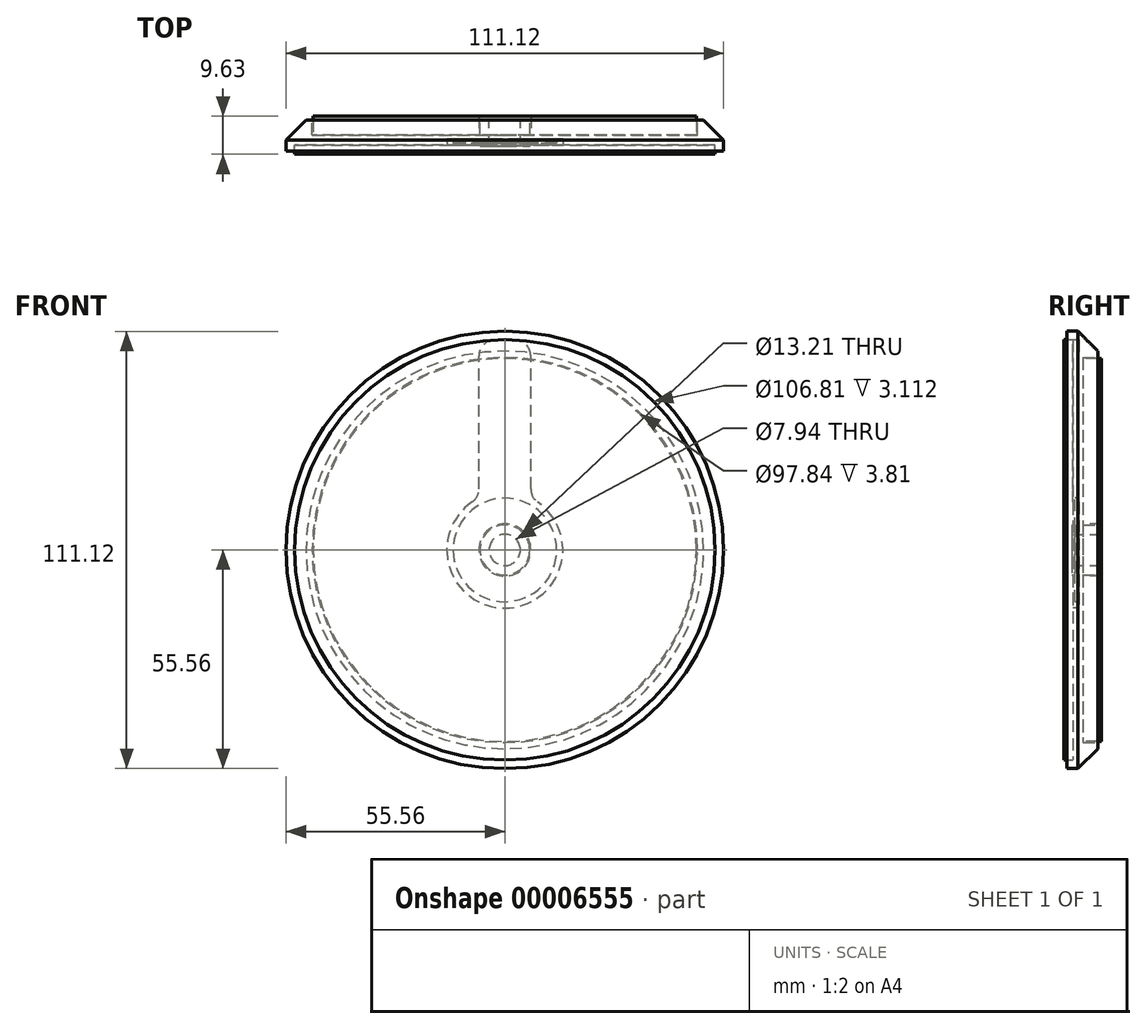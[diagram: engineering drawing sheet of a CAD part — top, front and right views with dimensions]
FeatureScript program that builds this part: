
annotation { "Feature Type Name" : "Feature", "Feature Type Description" : "" }
export const myFeature = defineFeature(function(context is Context, id is Id, definition is map)
    precondition{}
    {
        {
            var Q0;
            Q0=qCreatedBy(makeId("Top.planeOp"),FACE);
            var sketch = newSketch(context, id + "F0", { "sketchPlane" : qUnion([Q0])});
            skLineSegment(sketch, "E0.rect.bottom", {"start": v(0, -15.56) * mm, "end": v(-50.48, -15.56) * mm});
            skLineSegment(sketch, "E0.rect.top", {"start": v(55.56, 15.56) * mm, "end": v(9.98, 15.56) * mm});
            skLineSegment(sketch, "E0.rect.left", {"start": v(55.56, -15.56) * mm, "end": v(55.56, 15.56) * mm});
            skLineSegment(sketch, "E0.rect.right", {"start": v(-55.56, -10.48) * mm, "end": v(-55.56, 15.56) * mm});
            skPoint(sketch, "E0.rect.middle", {"position": v(0, 0) * mm});
            skLineSegment(sketch, "E1.rect.bottom", {"start": v(-4, -4.68) * mm, "end": v(-5.02, -4.68) * mm});
            skLineSegment(sketch, "E1.rect.right", {"start": v(-5.02, -4.68) * mm, "end": v(-5.02, -2.31) * mm});
            skPoint(sketch, "E1.rect.middle", {"position": v(0, -3.56) * mm});
            skLineSegment(sketch, "E2.rect.right", {"start": v(-8, 12.4) * mm, "end": v(-8, 16.42) * mm});
            skPoint(sketch, "E2.rect.middle", {"position": v(0, 14.4) * mm});
            skLineSegment(sketch, "E3.0", {"start": v(-9.98, 15.56) * mm, "end": v(-9.98, 16.42) * mm});
            skLineSegment(sketch, "E4.1", {"start": v(7, -7.04) * mm, "end": v(6.35, -7.04) * mm});
            skLineSegment(sketch, "E5", {"start": v(-9.98, 16.42) * mm, "end": v(-8, 16.42) * mm});
            skLineSegment(sketch, "E6.trimOffspring", {"start": v(-9.98, 15.56) * mm, "end": v(-49.34, 15.56) * mm});
            skLineSegment(sketch, "E7.rect.bottom", {"start": v(42.88, -12.38) * mm, "end": v(11.25, -12.38) * mm});
            skLineSegment(sketch, "E7.rect.top", {"start": v(42.88, 15.56) * mm, "end": v(11.25, 15.56) * mm});
            skLineSegment(sketch, "E7.rect.left", {"start": v(42.88, -12.38) * mm, "end": v(42.88, 15.56) * mm});
            skLineSegment(sketch, "E7.rect.right", {"start": v(11.25, -12.38) * mm, "end": v(11.25, 15.56) * mm});
            skPoint(sketch, "E7.rect.middle", {"position": v(27.06, 1.59) * mm});
            skLineSegment(sketch, "E8.rect.bottom", {"start": v(11.25, -9.41) * mm, "end": v(9.27, -9.41) * mm});
            skLineSegment(sketch, "E8.rect.top", {"start": v(11.25, 12.59) * mm, "end": v(9.27, 12.59) * mm});
            skLineSegment(sketch, "E8.rect.left", {"start": v(11.25, -9.41) * mm, "end": v(11.25, 12.59) * mm});
            skLineSegment(sketch, "E8.rect.right", {"start": v(9.27, -9.41) * mm, "end": v(9.27, 12.59) * mm});
            skPoint(sketch, "E8.rect.middle", {"position": v(10.26, 1.59) * mm});
            skLineSegment(sketch, "E9", {"start": v(10.26, 1.59) * mm, "end": v(-17.78, 1.59) * mm});
            skLineSegment(sketch, "E10", {"start": v(-55.56, -10.48) * mm, "end": v(-55.56, -9.46) * mm});
            skLineSegment(sketch, "E11", {"start": v(-55.56, -9.46) * mm, "end": v(-52.39, -9.46) * mm});
            skLineSegment(sketch, "E12", {"start": v(-52.39, -9.46) * mm, "end": v(-52.39, -6) * mm});
            skLineSegment(sketch, "E13", {"start": v(-52.39, -6) * mm, "end": v(-53.53, -6) * mm});
            skLineSegment(sketch, "E14", {"start": v(-53.53, -6) * mm, "end": v(-53.53, -4.42) * mm});
            skLineSegment(sketch, "E15", {"start": v(-53.53, -4.42) * mm, "end": v(-50.8, -4.42) * mm});
            skLineSegment(sketch, "E16", {"start": v(-50.8, -4.42) * mm, "end": v(-50.8, -13.02) * mm});
            skLineSegment(sketch, "E17", {"start": v(-50.8, -13.02) * mm, "end": v(-6.35, -13.02) * mm});
            skLineSegment(sketch, "E18", {"start": v(-53.66, -4.42) * mm, "end": v(-53.66, -9.46) * mm});
            skLineSegment(sketch, "E19", {"start": v(-55.56, -10.48) * mm, "end": v(-50.48, -15.56) * mm});
            skPoint(sketch, "E20.orphan", {"position": v(-55.56, -15.56) * mm});
            skLineSegment(sketch, "E21", {"start": v(55.56, -13.9) * mm, "end": v(4.5, -13.9) * mm});
            skLineSegment(sketch, "E22", {"start": v(-6.35, 16.68) * mm, "end": v(-48.32, 16.68) * mm});
            skLineSegment(sketch, "E23", {"start": v(-55.56, 17.97) * mm, "end": v(-50.5, 23.03) * mm});
            skPoint(sketch, "E24.orphan", {"position": v(-55.59, 23.03) * mm});
            skLineSegment(sketch, "E25.rect.bottom", {"start": v(-74.76, -10.55) * mm, "end": v(-76.24, -10.55) * mm});
            skLineSegment(sketch, "E25.rect.top", {"start": v(-74.76, 9.87) * mm, "end": v(-76.24, 9.87) * mm});
            skLineSegment(sketch, "E25.rect.left", {"start": v(-74.76, -10.55) * mm, "end": v(-74.76, 9.87) * mm});
            skLineSegment(sketch, "E25.rect.right", {"start": v(-76.24, -10.55) * mm, "end": v(-76.24, 9.87) * mm});
            skPoint(sketch, "E25.rect.middle", {"position": v(-75.5, -0.34) * mm});
            skLineSegment(sketch, "E26.bottom", {"start": v(-76.24, 7.41) * mm, "end": v(-74.76, 7.41) * mm});
            skLineSegment(sketch, "E26.top", {"start": v(-76.24, -3.8) * mm, "end": v(-74.76, -3.8) * mm});
            skLineSegment(sketch, "E26.left", {"start": v(-76.24, 7.41) * mm, "end": v(-76.24, -3.8) * mm});
            skLineSegment(sketch, "E26.right", {"start": v(-74.76, 7.41) * mm, "end": v(-74.76, -3.8) * mm});
            skLineSegment(sketch, "E27", {"start": v(-48.92, 23.03) * mm, "end": v(-48.92, 19.22) * mm});
            skLineSegment(sketch, "E28", {"start": v(-48.92, 19.22) * mm, "end": v(-6.35, 19.22) * mm});
            skLineSegment(sketch, "E29", {"start": v(-6.35, 19.22) * mm, "end": v(-6.35, 23.05) * mm});
            skLineSegment(sketch, "E30.trimOffspring", {"start": v(-6.35, 23.05) * mm, "end": v(-3.97, 23.05) * mm});
            skLineSegment(sketch, "E31", {"start": v(-50.5, 23.03) * mm, "end": v(-48.92, 23.03) * mm});
            skLineSegment(sketch, "E32", {"start": v(0, 23.05) * mm, "end": v(0, 16.68) * mm});
            skLineSegment(sketch, "E33", {"start": v(0, 12.42) * mm, "end": v(0, 9.24) * mm});
            skLineSegment(sketch, "E34", {"start": v(-53.53, -4.3) * mm, "end": v(-50.55, -4.3) * mm});
            skLineSegment(sketch, "E35", {"start": v(-53.53, -2.31) * mm, "end": v(-53.53, -4.3) * mm});
            skLineSegment(sketch, "E36", {"start": v(0, -4.68) * mm, "end": v(0, -7.04) * mm});
            skLineSegment(sketch, "E37", {"start": v(-45.33, 1.8) * mm, "end": v(-74.76, 1.8) * mm});
            skLineSegment(sketch, "E38", {"start": v(11.25, -10.9) * mm, "end": v(9.27, -10.9) * mm});
            skLineSegment(sketch, "E39", {"start": v(9.27, -10.9) * mm, "end": v(7.77, -10.9) * mm});
            skLineSegment(sketch, "E40", {"start": v(-55.56, 17.97) * mm, "end": v(-55.56, 15.11) * mm});
            skLineSegment(sketch, "E41.trimOffspring", {"start": v(0, -7.04) * mm, "end": v(-7, -7.04) * mm});
            skLineSegment(sketch, "E42", {"start": v(-74.76, 7.41) * mm, "end": v(-74.76, 10.59) * mm});
            skLineSegment(sketch, "E43", {"start": v(-53.66, -4.42) * mm, "end": v(-53.66, 10.16) * mm});
            skLineSegment(sketch, "E44", {"start": v(-55.56, 15.11) * mm, "end": v(-53.4, 15.11) * mm});
            skLineSegment(sketch, "E45", {"start": v(-53.4, 15.11) * mm, "end": v(-53.4, 16.68) * mm});
            skLineSegment(sketch, "E46", {"start": v(-55.56, 14.1) * mm, "end": v(-52.39, 14.1) * mm});
            skLineSegment(sketch, "E47", {"start": v(-52.39, 14.1) * mm, "end": v(-52.39, 15.56) * mm});
            skLineSegment(sketch, "E48", {"start": v(-52.39, 15.56) * mm, "end": v(-49.34, 15.56) * mm});
            skLineSegment(sketch, "E49", {"start": v(-48.32, 16.68) * mm, "end": v(-53.4, 16.68) * mm});
            skLineSegment(sketch, "E50", {"start": v(-6.35, 16.68) * mm, "end": v(-6.35, 16.42) * mm});
            skLineSegment(sketch, "E51", {"start": v(-6.35, 16.42) * mm, "end": v(-3.97, 16.42) * mm});
            skLineSegment(sketch, "E52", {"start": v(0, 16.42) * mm, "end": v(0, 16.68) * mm});
            skLineSegment(sketch, "E53", {"start": v(-7.56, -2.31) * mm, "end": v(-53.53, -2.31) * mm});
            skLineSegment(sketch, "E54", {"start": v(-50.55, -4.3) * mm, "end": v(-50.55, -5.87) * mm});
            skLineSegment(sketch, "E55", {"start": v(-50.55, -5.87) * mm, "end": v(-50.55, -7.04) * mm});
            skLineSegment(sketch, "E56", {"start": v(-50.55, -7.04) * mm, "end": v(-7, -7.04) * mm});
            skLineSegment(sketch, "E57", {"start": v(-6.35, -13.02) * mm, "end": v(-6.35, -7.62) * mm});
            skLineSegment(sketch, "E58", {"start": v(-6.35, -7.62) * mm, "end": v(-3.97, -7.62) * mm});
            skLineSegment(sketch, "E59", {"start": v(-45.33, 1.8) * mm, "end": v(-45.33, -2.31) * mm});
            skLineSegment(sketch, "E60", {"start": v(0, -7.62) * mm, "end": v(6.35, -7.62) * mm});
            skLineSegment(sketch, "E61", {"start": v(-4, -4.68) * mm, "end": v(-4, -4.93) * mm});
            skLineSegment(sketch, "E62", {"start": v(-4, -4.93) * mm, "end": v(0, -4.93) * mm});
            skLineSegment(sketch, "E63", {"start": v(-6.41, 12.4) * mm, "end": v(-6.41, 12.14) * mm});
            skLineSegment(sketch, "E64.trimOffspring", {"start": v(-6.41, 12.4) * mm, "end": v(-8, 12.4) * mm});
            skLineSegment(sketch, "E65", {"start": v(0, -1.42) * mm, "end": v(0, 10.58) * mm});
            skLineSegment(sketch, "E66", {"start": v(0, -1.42) * mm, "end": v(0, 4.58) * mm});
            skLineSegment(sketch, "E67", {"start": v(-6.41, 10.83) * mm, "end": v(-53.66, 10.83) * mm});
            skLineSegment(sketch, "E68", {"start": v(-53.66, 10.83) * mm, "end": v(-53.66, 10.16) * mm});
            skLineSegment(sketch, "E69", {"start": v(-5.02, -2.31) * mm, "end": v(-5.02, -1.68) * mm});
            skLineSegment(sketch, "E70", {"start": v(-5.02, -1.68) * mm, "end": v(-7.56, -1.68) * mm});
            skLineSegment(sketch, "E71", {"start": v(-7.56, -1.68) * mm, "end": v(-7.56, -2.31) * mm});
            skLineSegment(sketch, "E72", {"start": v(-6.41, 12.14) * mm, "end": v(-6.41, 10.83) * mm});
            skPoint(sketch, "E73.end.orphan", {"position": v(0, 12.14) * mm});
            skPoint(sketch, "E74.orphan", {"position": v(0, 10.83) * mm});
            skLineSegment(sketch, "E75", {"start": v(-3.97, 23.05) * mm, "end": v(-3.97, 16.42) * mm});
            skLineSegment(sketch, "E76", {"start": v(-3.97, -7.62) * mm, "end": v(-3.97, -15.56) * mm});
            skPoint(sketch, "E77.start.orphan", {"position": v(0, -13.02) * mm});
            skSolve(sketch);
        }
        {
            var Q0;
            Q0=makeQuery(id+"F0.imprint","IMPRINT",FACE,{"disambiguationData":[TD([[makeQuery(id+"F0.imprint","IMPRINT",EDGE,{"derivedFrom":sQuery(id+"F0.wireOp",EDGE,"E22")}),-1.0]])]});
            var Q1;
            Q1=sQuery(id+"F0.wireOp",EDGE,"E32");
            revolve(context, id + "F1", {"entities" : qUnion([Q0]), "axis" : qUnion([Q1]), "revolveType" : RevolveType.FULL});
        }
        {
            var Q0;
            Q0=makeQuery(id+"F1.opRevolve","SWEPT_FACE",FACE,{"disambiguationData":[OSD([sQuery(id+"F0.wireOp",EDGE,"E28")])]});
            var sketch = newSketch(context, id + "F2", { "sketchPlane" : qUnion([Q0])});
            skCircle(sketch, "E78.0", {"center": v(0, 0) * mm, "radius": 6.35 * mm});
            skCircle(sketch, "E79.0", {"center": v(0, 0) * mm, "radius": 48.92 * mm});
            skCircle(sketch, "E80.0", {"center": v(0, 0) * mm, "radius": 48.67 * mm});
            skCircle(sketch, "E81.0", {"center": v(0, 0) * mm, "radius": 6.6 * mm});
            skSolve(sketch);
        }
        {
            var Q0;
            Q0=makeQuery(id+"F2.imprint","IMPRINT",FACE,{"disambiguationData":[TD([[makeQuery(id+"F2.imprint","IMPRINT",EDGE,{"derivedFrom":sQuery(id+"F2.wireOp",EDGE,"E80.0")}),1.0]])]});
            extrude(context, id + "F3", {"entities" : qUnion([Q0]), "depth" : 4.76 * mm});
        }
        {
            var Q0;
            Q0=makeQuery(id+"F1.opRevolve","SWEPT_FACE",FACE,{"disambiguationData":[OSD([sQuery(id+"F0.wireOp",EDGE,"E44")])]});
            var sketch = newSketch(context, id + "F4", { "sketchPlane" : qUnion([Q0])});
            skSolve(sketch);
        }
        {
            var Q0;
            {var subQ0=sQuery(id+"F0.wireOp",EDGE,"E44");Q0=makeQuery(id+"F4.imprint","IMPRINT",FACE,{"disambiguationData":[TD([[makeQuery(id+"F4.imprint","IMPRINT",EDGE,{"derivedFrom":makeQuery(id+"F1.opRevolve","SWEPT_EDGE",EDGE,{"disambiguationData":[OSD([sQuery(id+"F0.wireOp",EDGE,"E40"),subQ0])]})}),-1.0]])]});}
            extrude(context, id + "F5", {"entities" : qUnion([Q0]), "operationType" : NewBodyOperationType.ADD, "depth" : 0.76 * mm});
        }
        {
            var Q0;
            Q0=makeQuery(id+"F1.opRevolve","SWEPT_FACE",FACE,{"disambiguationData":[OSD([sQuery(id+"F0.wireOp",EDGE,"E22"),sQuery(id+"F0.wireOp",EDGE,"E49")])]});
            var sketch = newSketch(context, id + "F6", { "sketchPlane" : qUnion([Q0])});
            skCircle(sketch, "E82", {"center": v(0, 0) * mm, "radius": 13.16 * mm});
            skSolve(sketch);
        }
        {
            var Q0;
            Q0=makeQuery(id+"F6.imprint","IMPRINT",FACE,{"disambiguationData":[TD([[makeQuery(id+"F6.imprint","IMPRINT",EDGE,{"derivedFrom":sQuery(id+"F6.wireOp",EDGE,"E82")}),1.0]])]});
            extrude(context, id + "F7", {"entities" : qUnion([Q0]), "operationType" : NewBodyOperationType.REMOVE, "oppositeDirection" : true, "depth" : 0.5 * mm});
        }
        {
            var Q0;
            Q0=makeQuery(id+"F1.opRevolve","SWEPT_FACE",FACE,{"disambiguationData":[OSD([sQuery(id+"F0.wireOp",EDGE,"E22"),sQuery(id+"F0.wireOp",EDGE,"E49")])]});
            var sketch = newSketch(context, id + "F8", { "sketchPlane" : qUnion([Q0])});
            skCircle(sketch, "E83.0", {"center": v(0, 0) * mm, "radius": 53.4 * mm});
            skArc(sketch, "E84.0", {"start": v(-6.6, 53) * mm, "mid": v(0, -53.4) * mm, "end": v(6.6, 53) * mm});
            skCircle(sketch, "E84.1", {"center": v(0, 0) * mm, "radius": 13.16 * mm});
            skArc(sketch, "E85.0", {"start": v(-6.6, 13.18) * mm, "mid": v(0, -14.74) * mm, "end": v(6.6, 13.18) * mm});
            skLineSegment(sketch, "E86.0", {"start": v(6.6, 13.18) * mm, "end": v(6.6, 53) * mm});
            skLineSegment(sketch, "E87.0", {"start": v(-6.6, 13.18) * mm, "end": v(-6.6, 53) * mm});
            skPoint(sketch, "E88.start.orphan", {"position": v(0, 14.74) * mm});
            skLineSegment(sketch, "E89.1.0", {"start": v(-6.19, 13.38) * mm, "end": v(-37.31, 38.2) * mm});
            skLineSegment(sketch, "E89.1.1", {"start": v(-14.42, 3.06) * mm, "end": v(-45.55, 27.88) * mm});
            skLineSegment(sketch, "E89.2.0", {"start": v(-14.32, 3.5) * mm, "end": v(-53.13, -5.35) * mm});
            skLineSegment(sketch, "E89.2.1", {"start": v(-11.38, -9.37) * mm, "end": v(-50.2, -18.23) * mm});
            skLineSegment(sketch, "E89.3.0", {"start": v(-11.67, -9.01) * mm, "end": v(-28.94, -44.88) * mm});
            skLineSegment(sketch, "E89.3.1", {"start": v(0.23, -14.74) * mm, "end": v(-17.04, -50.61) * mm});
            skLineSegment(sketch, "E89.4.0", {"start": v(-0.23, -14.74) * mm, "end": v(17.04, -50.61) * mm});
            skLineSegment(sketch, "E89.4.1", {"start": v(11.67, -9.01) * mm, "end": v(28.94, -44.88) * mm});
            skLineSegment(sketch, "E89.5.0", {"start": v(11.38, -9.37) * mm, "end": v(50.2, -18.23) * mm});
            skLineSegment(sketch, "E89.5.1", {"start": v(14.32, 3.5) * mm, "end": v(53.13, -5.35) * mm});
            skLineSegment(sketch, "E89.6.0", {"start": v(14.42, 3.06) * mm, "end": v(45.55, 27.88) * mm});
            skLineSegment(sketch, "E89.6.1", {"start": v(6.19, 13.38) * mm, "end": v(37.31, 38.2) * mm});
            skSolve(sketch);
        }
        {
            var Q0;
            {var subQ1=sQuery(id+"F8.wireOp",EDGE,"E87.0");var subQ3=sQuery(id+"F8.wireOp",EDGE,"E83.0");var subQ5=makeQuery(id+"F8.imprint","INTERSECT",VERTEX,{"derivedFrom":[subQ3,subQ1]});Q0=makeQuery(id+"F8.imprint","IMPRINT",FACE,{"disambiguationData":[TD([[makeQuery(id+"F8.imprint","IMPRINT",EDGE,{"disambiguationData":[TD([[subQ5,1.0]])],"derivedFrom":subQ3}),-1.0]])]});}
            var Q1;
            {var subQ1=sQuery(id+"F8.wireOp",EDGE,"E86.0");var subQ3=sQuery(id+"F8.wireOp",EDGE,"E83.0");var subQ5=makeQuery(id+"F8.imprint","INTERSECT",VERTEX,{"derivedFrom":[subQ3,subQ1]});Q1=makeQuery(id+"F8.imprint","IMPRINT",FACE,{"disambiguationData":[TD([[makeQuery(id+"F8.imprint","IMPRINT",EDGE,{"disambiguationData":[TD([[subQ5,-1.0]])],"derivedFrom":subQ3}),-1.0]])]});}
            var Q2;
            {var subQ1=sQuery(id+"F8.wireOp",EDGE,"E89.5.1");var subQ3=sQuery(id+"F8.wireOp",EDGE,"E83.0");var subQ5=makeQuery(id+"F8.imprint","INTERSECT",VERTEX,{"derivedFrom":[subQ3,subQ1]});Q2=makeQuery(id+"F8.imprint","IMPRINT",FACE,{"disambiguationData":[TD([[makeQuery(id+"F8.imprint","IMPRINT",EDGE,{"disambiguationData":[TD([[subQ5,1.0]])],"derivedFrom":subQ3}),-1.0]])]});}
            var Q3;
            {var subQ1=sQuery(id+"F8.wireOp",EDGE,"E89.4.1");var subQ3=sQuery(id+"F8.wireOp",EDGE,"E83.0");var subQ5=makeQuery(id+"F8.imprint","INTERSECT",VERTEX,{"derivedFrom":[subQ3,subQ1]});Q3=makeQuery(id+"F8.imprint","IMPRINT",FACE,{"disambiguationData":[TD([[makeQuery(id+"F8.imprint","IMPRINT",EDGE,{"disambiguationData":[TD([[subQ5,1.0]])],"derivedFrom":subQ3}),-1.0]])]});}
            var Q4;
            {var subQ1=sQuery(id+"F8.wireOp",EDGE,"E89.3.1");var subQ3=sQuery(id+"F8.wireOp",EDGE,"E83.0");var subQ5=makeQuery(id+"F8.imprint","INTERSECT",VERTEX,{"derivedFrom":[subQ3,subQ1]});Q4=makeQuery(id+"F8.imprint","IMPRINT",FACE,{"disambiguationData":[TD([[makeQuery(id+"F8.imprint","IMPRINT",EDGE,{"disambiguationData":[TD([[subQ5,1.0]])],"derivedFrom":subQ3}),-1.0]])]});}
            var Q5;
            {var subQ1=sQuery(id+"F8.wireOp",EDGE,"E89.2.1");var subQ3=sQuery(id+"F8.wireOp",EDGE,"E83.0");var subQ5=makeQuery(id+"F8.imprint","INTERSECT",VERTEX,{"derivedFrom":[subQ3,subQ1]});Q5=makeQuery(id+"F8.imprint","IMPRINT",FACE,{"disambiguationData":[TD([[makeQuery(id+"F8.imprint","IMPRINT",EDGE,{"disambiguationData":[TD([[subQ5,1.0]])],"derivedFrom":subQ3}),-1.0]])]});}
            var Q6;
            {var subQ1=sQuery(id+"F8.wireOp",EDGE,"E89.1.1");var subQ3=sQuery(id+"F8.wireOp",EDGE,"E83.0");var subQ5=makeQuery(id+"F8.imprint","INTERSECT",VERTEX,{"derivedFrom":[subQ3,subQ1]});Q6=makeQuery(id+"F8.imprint","IMPRINT",FACE,{"disambiguationData":[TD([[makeQuery(id+"F8.imprint","IMPRINT",EDGE,{"disambiguationData":[TD([[subQ5,1.0]])],"derivedFrom":subQ3}),-1.0]])]});}
            extrude(context, id + "F9", {"entities" : qUnion([Q0, Q1, Q2, Q3, Q4, Q5, Q6]), "operationType" : NewBodyOperationType.REMOVE, "oppositeDirection" : true, "depth" : 1.55 * mm});
        }
        {
            var Q0;
            Q0=makeQuery(id+"F9.boolean.opBoolean","COPY",EDGE,{"derivedFrom":makeQuery(id+"F9.opExtrude","SWEPT_EDGE",EDGE,{"disambiguationData":[OSD([sQuery(id+"F8.wireOp",EDGE,"E83.0"),sQuery(id+"F8.wireOp",EDGE,"E86.0")])]})});
            var Q1;
            Q1=makeQuery(id+"F9.boolean.opBoolean","COPY",EDGE,{"derivedFrom":makeQuery(id+"F9.opExtrude","SWEPT_EDGE",EDGE,{"disambiguationData":[OSD([sQuery(id+"F8.wireOp",EDGE,"E83.0"),sQuery(id+"F8.wireOp",EDGE,"E89.6.0")])]})});
            var Q2;
            Q2=makeQuery(id+"F9.boolean.opBoolean","COPY",EDGE,{"derivedFrom":makeQuery(id+"F9.opExtrude","SWEPT_EDGE",EDGE,{"disambiguationData":[OSD([sQuery(id+"F8.wireOp",EDGE,"E83.0"),sQuery(id+"F8.wireOp",EDGE,"E89.5.0")])]})});
            var Q3;
            Q3=makeQuery(id+"F9.boolean.opBoolean","COPY",EDGE,{"derivedFrom":makeQuery(id+"F9.opExtrude","SWEPT_EDGE",EDGE,{"disambiguationData":[OSD([sQuery(id+"F8.wireOp",EDGE,"E83.0"),sQuery(id+"F8.wireOp",EDGE,"E89.4.0")])]})});
            var Q4;
            Q4=makeQuery(id+"F9.boolean.opBoolean","COPY",EDGE,{"derivedFrom":makeQuery(id+"F9.opExtrude","SWEPT_EDGE",EDGE,{"disambiguationData":[OSD([sQuery(id+"F8.wireOp",EDGE,"E83.0"),sQuery(id+"F8.wireOp",EDGE,"E89.3.0")])]})});
            var Q5;
            Q5=makeQuery(id+"F9.boolean.opBoolean","COPY",EDGE,{"derivedFrom":makeQuery(id+"F9.opExtrude","SWEPT_EDGE",EDGE,{"disambiguationData":[OSD([sQuery(id+"F8.wireOp",EDGE,"E83.0"),sQuery(id+"F8.wireOp",EDGE,"E89.2.0")])]})});
            var Q6;
            Q6=makeQuery(id+"F9.boolean.opBoolean","COPY",EDGE,{"derivedFrom":makeQuery(id+"F9.opExtrude","SWEPT_EDGE",EDGE,{"disambiguationData":[OSD([sQuery(id+"F8.wireOp",EDGE,"E83.0"),sQuery(id+"F8.wireOp",EDGE,"E89.1.0")])]})});
            var Q7;
            Q7=makeQuery(id+"F9.boolean.opBoolean","COPY",EDGE,{"derivedFrom":makeQuery(id+"F9.opExtrude","SWEPT_EDGE",EDGE,{"disambiguationData":[OSD([sQuery(id+"F8.wireOp",EDGE,"E83.0"),sQuery(id+"F8.wireOp",EDGE,"E89.6.1")])]})});
            var Q8;
            Q8=makeQuery(id+"F9.boolean.opBoolean","COPY",EDGE,{"derivedFrom":makeQuery(id+"F9.opExtrude","SWEPT_EDGE",EDGE,{"disambiguationData":[OSD([sQuery(id+"F8.wireOp",EDGE,"E83.0"),sQuery(id+"F8.wireOp",EDGE,"E89.5.1")])]})});
            var Q9;
            Q9=makeQuery(id+"F9.boolean.opBoolean","COPY",EDGE,{"derivedFrom":makeQuery(id+"F9.opExtrude","SWEPT_EDGE",EDGE,{"disambiguationData":[OSD([sQuery(id+"F8.wireOp",EDGE,"E83.0"),sQuery(id+"F8.wireOp",EDGE,"E89.4.1")])]})});
            var Q10;
            Q10=makeQuery(id+"F9.boolean.opBoolean","COPY",EDGE,{"derivedFrom":makeQuery(id+"F9.opExtrude","SWEPT_EDGE",EDGE,{"disambiguationData":[OSD([sQuery(id+"F8.wireOp",EDGE,"E83.0"),sQuery(id+"F8.wireOp",EDGE,"E89.3.1")])]})});
            var Q11;
            Q11=makeQuery(id+"F9.boolean.opBoolean","COPY",EDGE,{"derivedFrom":makeQuery(id+"F9.opExtrude","SWEPT_EDGE",EDGE,{"disambiguationData":[OSD([sQuery(id+"F8.wireOp",EDGE,"E83.0"),sQuery(id+"F8.wireOp",EDGE,"E89.2.1")])]})});
            var Q12;
            Q12=makeQuery(id+"F9.boolean.opBoolean","COPY",EDGE,{"derivedFrom":makeQuery(id+"F9.opExtrude","SWEPT_EDGE",EDGE,{"disambiguationData":[OSD([sQuery(id+"F8.wireOp",EDGE,"E83.0"),sQuery(id+"F8.wireOp",EDGE,"E89.1.1")])]})});
            var Q13;
            Q13=makeQuery(id+"F9.boolean.opBoolean","COPY",EDGE,{"derivedFrom":makeQuery(id+"F9.opExtrude","SWEPT_EDGE",EDGE,{"disambiguationData":[OSD([sQuery(id+"F8.wireOp",EDGE,"E83.0"),sQuery(id+"F8.wireOp",EDGE,"E87.0")])]})});
            var Q14;
            Q14=makeQuery(id+"F9.boolean.opBoolean","COPY",EDGE,{"derivedFrom":makeQuery(id+"F9.opExtrude","SWEPT_EDGE",EDGE,{"disambiguationData":[OSD([sQuery(id+"F8.wireOp",EDGE,"E87.0"),sQuery(id+"F8.wireOp",EDGE,"E89.1.0")])]})});
            var Q15;
            Q15=makeQuery(id+"F9.boolean.opBoolean","COPY",EDGE,{"derivedFrom":makeQuery(id+"F9.opExtrude","SWEPT_EDGE",EDGE,{"disambiguationData":[OSD([sQuery(id+"F8.wireOp",EDGE,"E89.1.1"),sQuery(id+"F8.wireOp",EDGE,"E89.2.0")])]})});
            var Q16;
            Q16=makeQuery(id+"F9.boolean.opBoolean","COPY",EDGE,{"derivedFrom":makeQuery(id+"F9.opExtrude","SWEPT_EDGE",EDGE,{"disambiguationData":[OSD([sQuery(id+"F8.wireOp",EDGE,"E89.2.1"),sQuery(id+"F8.wireOp",EDGE,"E89.3.0")])]})});
            var Q17;
            Q17=makeQuery(id+"F9.boolean.opBoolean","COPY",EDGE,{"derivedFrom":makeQuery(id+"F9.opExtrude","SWEPT_EDGE",EDGE,{"disambiguationData":[OSD([sQuery(id+"F8.wireOp",EDGE,"E89.3.1"),sQuery(id+"F8.wireOp",EDGE,"E89.4.0")])]})});
            var Q18;
            Q18=makeQuery(id+"F9.boolean.opBoolean","COPY",EDGE,{"derivedFrom":makeQuery(id+"F9.opExtrude","SWEPT_EDGE",EDGE,{"disambiguationData":[OSD([sQuery(id+"F8.wireOp",EDGE,"E89.4.1"),sQuery(id+"F8.wireOp",EDGE,"E89.5.0")])]})});
            var Q19;
            Q19=makeQuery(id+"F9.boolean.opBoolean","COPY",EDGE,{"derivedFrom":makeQuery(id+"F9.opExtrude","SWEPT_EDGE",EDGE,{"disambiguationData":[OSD([sQuery(id+"F8.wireOp",EDGE,"E89.5.1"),sQuery(id+"F8.wireOp",EDGE,"E89.6.0")])]})});
            var Q20;
            Q20=makeQuery(id+"F9.boolean.opBoolean","COPY",EDGE,{"derivedFrom":makeQuery(id+"F9.opExtrude","SWEPT_EDGE",EDGE,{"disambiguationData":[OSD([sQuery(id+"F8.wireOp",EDGE,"E86.0"),sQuery(id+"F8.wireOp",EDGE,"E89.6.1")])]})});
            fillet(context, id + "F10", {"entities" : qUnion([Q0, Q1, Q2, Q3, Q4, Q5, Q6, Q7, Q8, Q9, Q10, Q11, Q12, Q13, Q14, Q15, Q16, Q17, Q18, Q19, Q20]), "radius" : 4.06 * mm, "tangentPropagation" : true, "allowEdgeOverflow" : false});
        }
    });
